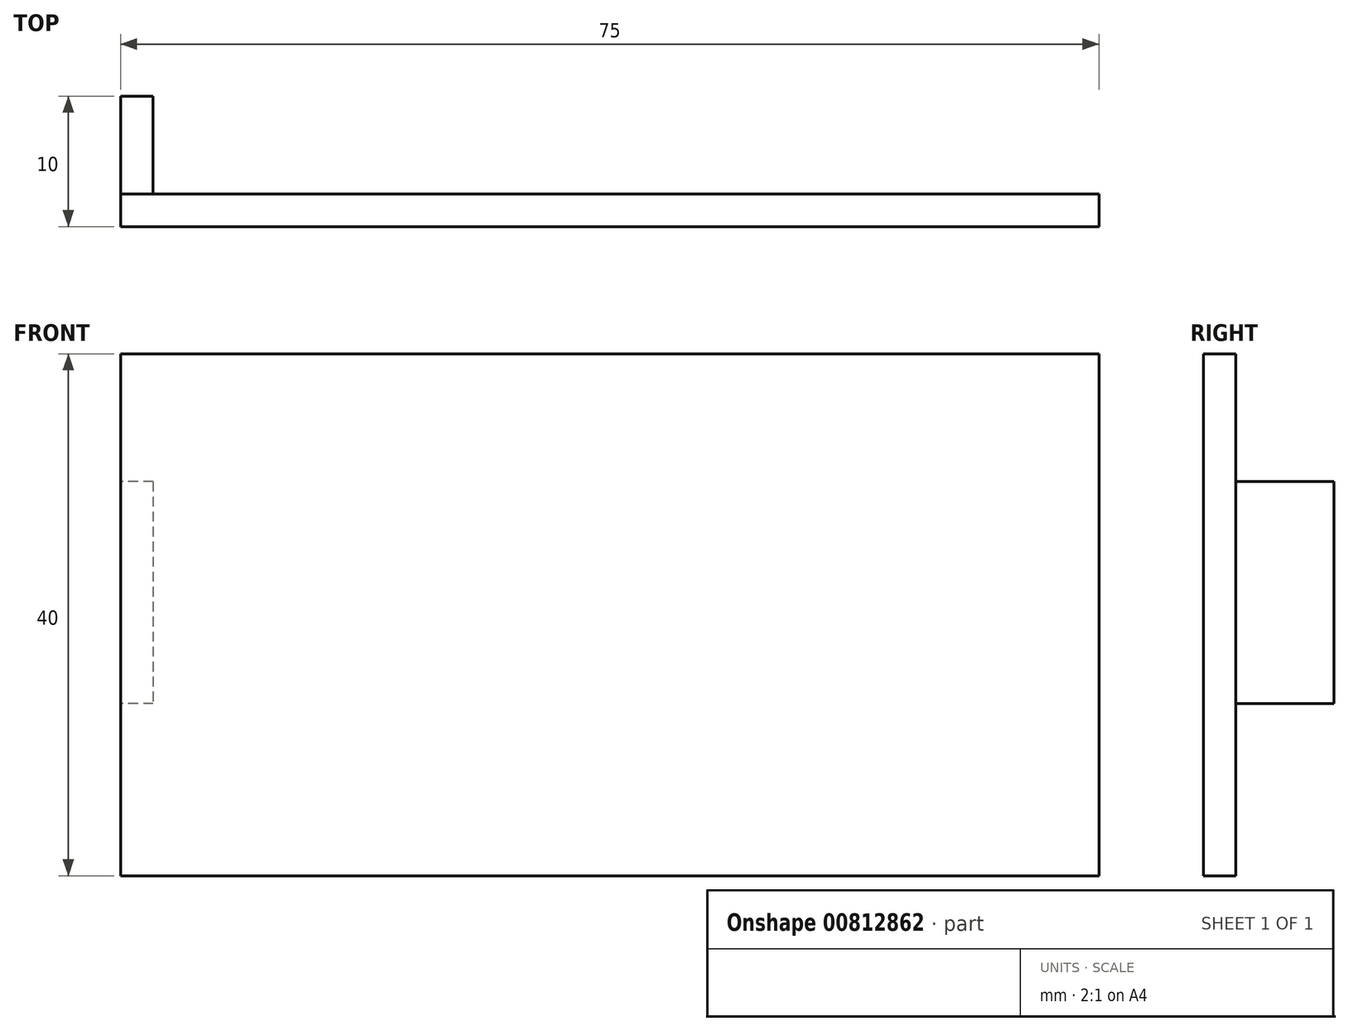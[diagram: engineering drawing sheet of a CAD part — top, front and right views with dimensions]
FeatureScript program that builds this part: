
annotation { "Feature Type Name" : "Feature", "Feature Type Description" : "" }
export const myFeature = defineFeature(function(context is Context, id is Id, definition is map)
    precondition{}
    {
        {
            var Q0;
            Q0=qCreatedBy(makeId("Front.planeOp"),FACE);
            var sketch = newSketch(context, id + "F0", { "sketchPlane" : qUnion([Q0])});
            skLineSegment(sketch, "E0.bottom", {"start": v(-37.5, 20) * mm, "end": v(37.5, 20) * mm});
            skLineSegment(sketch, "E0.top", {"start": v(-37.5, -20) * mm, "end": v(37.5, -20) * mm});
            skLineSegment(sketch, "E0.left", {"start": v(-37.5, 20) * mm, "end": v(-37.5, -20) * mm});
            skLineSegment(sketch, "E0.right", {"start": v(37.5, 20) * mm, "end": v(37.5, -20) * mm});
            skPoint(sketch, "E0.middle", {"position": v(0, 0) * mm});
            skLineSegment(sketch, "E1.bottom", {"start": v(-35, 17.5) * mm, "end": v(35, 17.5) * mm});
            skLineSegment(sketch, "E1.top", {"start": v(-35, -17.5) * mm, "end": v(35, -17.5) * mm});
            skLineSegment(sketch, "E1.left", {"start": v(-35, 17.5) * mm, "end": v(-35, -17.5) * mm});
            skLineSegment(sketch, "E1.right", {"start": v(35, 17.5) * mm, "end": v(35, -17.5) * mm});
            skLineSegment(sketch, "E2", {"start": v(-35, 17.5) * mm, "end": v(-35, 10.2) * mm});
            skLineSegment(sketch, "E3", {"start": v(-35, -17.5) * mm, "end": v(-35, -6.8) * mm});
            skLineSegment(sketch, "E4", {"start": v(-35, -6.8) * mm, "end": v(-37.5, -6.8) * mm});
            skLineSegment(sketch, "E5", {"start": v(-35, 10.2) * mm, "end": v(-37.5, 10.2) * mm});
            skSolve(sketch);
        }
        {
            var Q0;
            Q0 = qSketchRegion(id + "F0", true);
            var Q1;
            Q1=makeQuery(id+"F0.imprint","IMPRINT",FACE,{"disambiguationData":[TD([[makeQuery(id+"F0.imprint","IMPRINT",EDGE,{"derivedFrom":sQuery(id+"F0.wireOp",EDGE,"E1.bottom")}),-1.0]])]});
            var Q2;
            Q2=makeQuery(id+"F0.imprint","IMPRINT",FACE,{"disambiguationData":[TD([[makeQuery(id+"F0.imprint","IMPRINT",EDGE,{"derivedFrom":sQuery(id+"F0.wireOp",EDGE,"gzSXawoP-ZyPa-Vn3G-gN8q-fJpea5gHBbJ8")}),-1.0]])]});
            var Q3;
            Q3=makeQuery(id+"F0.imprint","IMPRINT",FACE,{"disambiguationData":[TD([[makeQuery(id+"F0.imprint","IMPRINT",EDGE,{"derivedFrom":sQuery(id+"F0.wireOp",EDGE,"725b1791-586d-44e4-acb8-3ff94516d762")}),-1.0]])]});
            var Q4;
            Q4=makeQuery(id+"F0.imprint","IMPRINT",FACE,{"disambiguationData":[TD([[makeQuery(id+"F0.imprint","IMPRINT",EDGE,{"derivedFrom":sQuery(id+"F0.wireOp",EDGE,"925ba65e-411a-4005-894b-690ae9a2de90")}),-1.0]])]});
            var Q5;
            Q5=makeQuery(id+"F0.imprint","IMPRINT",FACE,{"disambiguationData":[TD([[makeQuery(id+"F0.imprint","IMPRINT",EDGE,{"derivedFrom":sQuery(id+"F0.wireOp",EDGE,"1d9f5036-cd0a-4186-a8e9-d76069c8db17")}),-1.0]])]});
            var Q6;
            Q6=makeQuery(id+"F0.imprint","IMPRINT",FACE,{"disambiguationData":[TD([[makeQuery(id+"F0.imprint","IMPRINT",EDGE,{"derivedFrom":sQuery(id+"F0.wireOp",EDGE,"gzSXawoP-ZyPa-Vn3G-gN8q-fJpea5gHBbJ8")}),1.0]])]});
            var Q7;
            Q7=makeQuery(id+"F0.imprint","IMPRINT",FACE,{"disambiguationData":[TD([[makeQuery(id+"F0.imprint","IMPRINT",EDGE,{"derivedFrom":sQuery(id+"F0.wireOp",EDGE,"725b1791-586d-44e4-acb8-3ff94516d762")}),1.0]])]});
            var Q8;
            Q8=makeQuery(id+"F0.imprint","IMPRINT",FACE,{"disambiguationData":[TD([[makeQuery(id+"F0.imprint","IMPRINT",EDGE,{"derivedFrom":sQuery(id+"F0.wireOp",EDGE,"925ba65e-411a-4005-894b-690ae9a2de90")}),1.0]])]});
            var Q9;
            Q9=makeQuery(id+"F0.imprint","IMPRINT",FACE,{"disambiguationData":[TD([[makeQuery(id+"F0.imprint","IMPRINT",EDGE,{"derivedFrom":sQuery(id+"F0.wireOp",EDGE,"1d9f5036-cd0a-4186-a8e9-d76069c8db17")}),1.0]])]});
            extrude(context, id + "F1", {"entities" : qUnion([Q0, Q1, Q2, Q3, Q4, Q5, Q6, Q7, Q8, Q9]), "depth" : 10 * mm, "offsetDistance" : 25 * mm});
        }
        {
            var Q0;
            Q0=makeQuery(id+"F0.imprint","IMPRINT",FACE,{"disambiguationData":[TD([[makeQuery(id+"F0.imprint","IMPRINT",EDGE,{"derivedFrom":sQuery(id+"F0.wireOp",EDGE,"E1.bottom")}),-1.0]])]});
            var Q1;
            Q1=makeQuery(id+"F0.imprint","IMPRINT",FACE,{"disambiguationData":[TD([[makeQuery(id+"F0.imprint","IMPRINT",EDGE,{"derivedFrom":sQuery(id+"F0.wireOp",EDGE,"1d9f5036-cd0a-4186-a8e9-d76069c8db17")}),1.0]])]});
            var Q2;
            Q2=makeQuery(id+"F0.imprint","IMPRINT",FACE,{"disambiguationData":[TD([[makeQuery(id+"F0.imprint","IMPRINT",EDGE,{"derivedFrom":sQuery(id+"F0.wireOp",EDGE,"925ba65e-411a-4005-894b-690ae9a2de90")}),1.0]])]});
            var Q3;
            Q3=makeQuery(id+"F0.imprint","IMPRINT",FACE,{"disambiguationData":[TD([[makeQuery(id+"F0.imprint","IMPRINT",EDGE,{"derivedFrom":sQuery(id+"F0.wireOp",EDGE,"725b1791-586d-44e4-acb8-3ff94516d762")}),1.0]])]});
            var Q4;
            Q4=makeQuery(id+"F0.imprint","IMPRINT",FACE,{"disambiguationData":[TD([[makeQuery(id+"F0.imprint","IMPRINT",EDGE,{"derivedFrom":sQuery(id+"F0.wireOp",EDGE,"gzSXawoP-ZyPa-Vn3G-gN8q-fJpea5gHBbJ8")}),1.0]])]});
            var Q5;
            Q5=makeQuery(id+"F0.imprint","IMPRINT",FACE,{"disambiguationData":[TD([[makeQuery(id+"F0.imprint","IMPRINT",EDGE,{"derivedFrom":sQuery(id+"F0.wireOp",EDGE,"E1.left")}),-1.0]])]});
            extrude(context, id + "F2", {"entities" : qUnion([Q0, Q1, Q2, Q3, Q4, Q5]), "operationType" : NewBodyOperationType.REMOVE, "depth" : 7.5 * mm, "offsetDistance" : 25 * mm});
        }
    });
